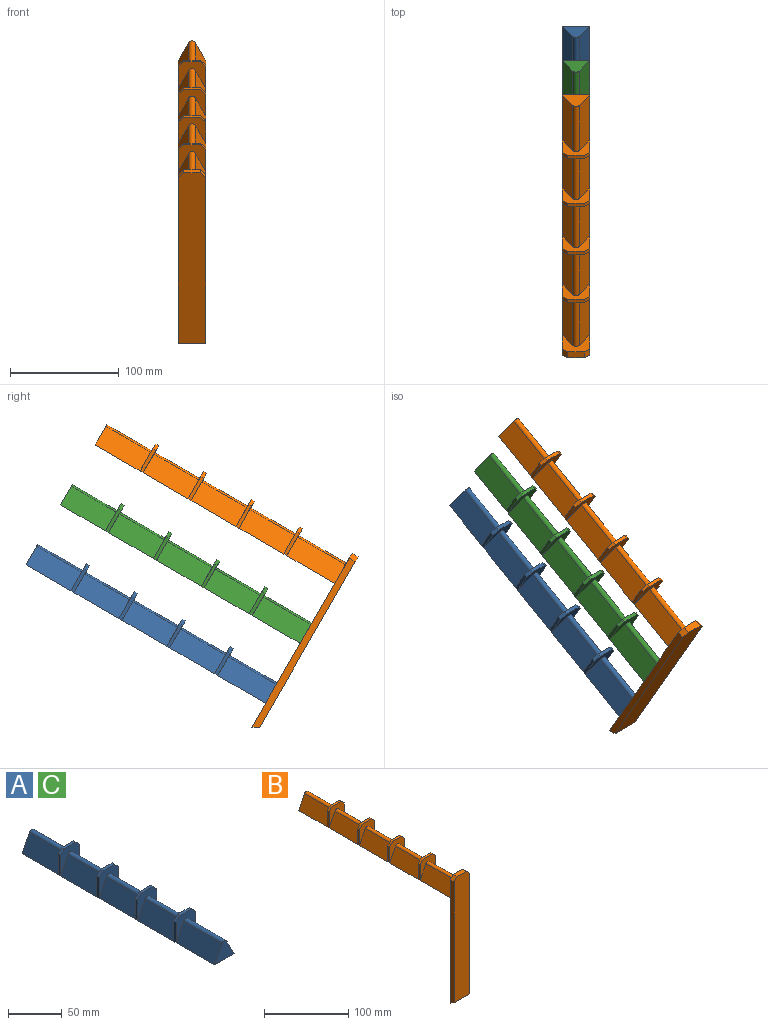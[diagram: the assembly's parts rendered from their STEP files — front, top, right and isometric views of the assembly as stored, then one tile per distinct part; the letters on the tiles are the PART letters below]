
ASSEMBLY  parts=3 mates=2
PART A: 46 faces, bbox 25.4x254x28.6 mm
  f0: plane 47.63x19.72mm, normal (0.89,0,0.45), area 1050mm2, adj f10,f23,f29,f33
  f1: plane 47.63x19.72mm, normal (-0.89,0,0.45), area 1050mm2, adj f10,f23,f29,f33
  f2: plane 47.63x19.72mm, normal (0.89,0,0.45), area 1050mm2, adj f10,f13,f24,f34
  f3: plane 47.63x19.72mm, normal (-0.89,0,0.45), area 1050mm2, adj f10,f13,f24,f34
  f4: plane 47.63x19.72mm, normal (0.89,0,0.45), area 1050mm2, adj f10,f19,f28,f35
  f5: plane 47.63x19.72mm, normal (-0.89,0,0.45), area 1050mm2, adj f10,f19,f28,f35
  f6: plane 50.8x19.72mm, normal (0.89,0,0.45), area 1120mm2, adj f8,f10,f14,f36
  f7: plane 50.8x19.72mm, normal (-0.89,0,0.45), area 1120mm2, adj f8,f10,f14,f36
  f8: plane 25.4x21.48mm, normal (0,-1,0), area 313.6mm2, adj f6,f7,f10,f36
  f9: plane 25.4x21.48mm, normal (0,1,0), area 313.6mm2, adj f10,f11,f12,f37
  f10: plane 254x25.4mm, normal (0,0,-1), area 6451.6mm2, adj f0,f1,f2,f3,f4,f5,f6,f7
  f11: plane 47.63x19.72mm, normal (0.89,0,0.45), area 1050mm2, adj f9,f10,f18,f37
  f12: plane 47.63x19.72mm, normal (-0.89,0,0.45), area 1050mm2, adj f9,f10,f18,f37
  f13: plane 28.58x25.4mm, normal (0,1,0), area 386.4mm2, adj f2,f3,f15,f16,f17,f34,f44,f45
  f14: plane 28.58x25.4mm, normal (0,-1,0), area 386.4mm2, adj f6,f7,f15,f16,f17,f36,f44,f45
  f15: plane 23.5x3.18mm, normal (-1,0,0), area 74.6mm2, adj f10,f13,f14,f45
  f16: plane 23.5x3.18mm, normal (1,0,0), area 74.6mm2, adj f10,f13,f14,f44
  f17: plane 15.24x3.18mm, normal (0,0,1), area 48.4mm2, adj f13,f14,f44,f45
  f18: plane 28.58x25.4mm, normal (0,1,0), area 386.4mm2, adj f11,f12,f20,f21,f22,f37,f40,f41
  f19: plane 28.58x25.4mm, normal (0,-1,0), area 386.4mm2, adj f4,f5,f20,f21,f22,f35,f40,f41
  f20: plane 23.5x3.18mm, normal (-1,0,0), area 74.6mm2, adj f10,f18,f19,f41
  f21: plane 23.5x3.18mm, normal (1,0,0), area 74.6mm2, adj f10,f18,f19,f40
  f22: plane 15.24x3.18mm, normal (0,0,1), area 48.4mm2, adj f18,f19,f40,f41
  f23: plane 28.58x25.4mm, normal (0,1,0), area 386.4mm2, adj f0,f1,f25,f26,f27,f33,f42,f43
  f24: plane 28.58x25.4mm, normal (0,-1,0), area 386.4mm2, adj f2,f3,f25,f26,f27,f34,f42,f43
  f25: plane 23.5x3.18mm, normal (-1,0,0), area 74.6mm2, adj f10,f23,f24,f43
  f26: plane 23.5x3.18mm, normal (1,0,0), area 74.6mm2, adj f10,f23,f24,f42
  f27: plane 15.24x3.18mm, normal (0,0,1), area 48.4mm2, adj f23,f24,f42,f43
  f28: plane 28.58x25.4mm, normal (0,1,0), area 386.4mm2, adj f4,f5,f30,f31,f32,f35,f38,f39
  f29: plane 28.58x25.4mm, normal (0,-1,0), area 386.4mm2, adj f0,f1,f30,f31,f32,f33,f38,f39
  f30: plane 23.5x3.18mm, normal (-1,0,0), area 74.6mm2, adj f10,f28,f29,f39
  f31: plane 23.5x3.18mm, normal (1,0,0), area 74.6mm2, adj f10,f28,f29,f38
  f32: plane 15.24x3.18mm, normal (0,0,1), area 48.4mm2, adj f28,f29,f38,f39
  f33: cylinder r=3.17mm len=47.63mm, axis (0,-1,0), area 334.8mm2, adj f0,f1,f23,f29
  f34: cylinder r=3.17mm len=47.63mm, axis (0,-1,0), area 334.8mm2, adj f2,f3,f13,f24
  f35: cylinder r=3.17mm len=47.63mm, axis (0,-1,0), area 334.8mm2, adj f4,f5,f19,f28
  f36: cylinder r=3.17mm len=50.8mm, axis (0,-1,0), area 357.1mm2, adj f6,f7,f8,f14
  f37: cylinder r=3.17mm len=47.63mm, axis (0,-1,0), area 334.8mm2, adj f9,f11,f12,f18
  f38: plane 5.08x5.08mm, normal (0.71,0,0.71), area 22.8mm2, adj f28,f29,f31,f32
  f39: plane 5.08x5.08mm, normal (-0.71,0,0.71), area 22.8mm2, adj f28,f29,f30,f32
  f40: plane 5.08x5.08mm, normal (0.71,0,0.71), area 22.8mm2, adj f18,f19,f21,f22
  f41: plane 5.08x5.08mm, normal (-0.71,0,0.71), area 22.8mm2, adj f18,f19,f20,f22
  f42: plane 5.08x5.08mm, normal (0.71,0,0.71), area 22.8mm2, adj f23,f24,f26,f27
  f43: plane 5.08x5.08mm, normal (-0.71,0,0.71), area 22.8mm2, adj f23,f24,f25,f27
  f44: plane 5.08x5.08mm, normal (0.71,0,0.71), area 22.8mm2, adj f13,f14,f16,f17
  f45: plane 5.08x5.08mm, normal (-0.71,0,0.71), area 22.8mm2, adj f13,f14,f15,f17
PART B: 54 faces, bbox 25.4x260.4x184.2 mm
  f0: plane 179.07x6.35mm, normal (1,0,0), area 1125.5mm2, adj f39,f40,f50,f52,f53
  f1: plane 254x25.4mm, normal (0,0,-1), area 6451.6mm2, adj f2,f3,f4,f5,f6,f7,f8,f9
  f2: plane 47.63x19.72mm, normal (0.89,0,0.45), area 1050mm2, adj f1,f23,f29,f33
  f3: plane 47.63x19.72mm, normal (-0.89,0,0.45), area 1050mm2, adj f1,f23,f29,f33
  f4: plane 47.63x19.72mm, normal (0.89,0,0.45), area 1050mm2, adj f1,f13,f24,f34
  f5: plane 47.63x19.72mm, normal (-0.89,0,0.45), area 1050mm2, adj f1,f13,f24,f34
  f6: plane 47.63x19.72mm, normal (0.89,0,0.45), area 1050mm2, adj f1,f19,f28,f35
  f7: plane 47.63x19.72mm, normal (-0.89,0,0.45), area 1050mm2, adj f1,f19,f28,f35
  f8: plane 50.8x19.72mm, normal (0.89,0,0.45), area 1120mm2, adj f1,f14,f36,f40
  f9: plane 50.8x19.72mm, normal (-0.89,0,0.45), area 1120mm2, adj f1,f14,f36,f40
  f10: plane 25.4x21.48mm, normal (0,1,0), area 313.6mm2, adj f1,f11,f12,f37
  f11: plane 47.63x19.72mm, normal (0.89,0,0.45), area 1050mm2, adj f1,f10,f18,f37
  f12: plane 47.63x19.72mm, normal (-0.89,0,0.45), area 1050mm2, adj f1,f10,f18,f37
  f13: plane 28.58x25.4mm, normal (0,1,0), area 386.4mm2, adj f4,f5,f15,f16,f17,f34,f48,f49
  f14: plane 28.58x25.4mm, normal (0,-1,0), area 386.4mm2, adj f8,f9,f15,f16,f17,f36,f48,f49
  f15: plane 23.5x3.18mm, normal (-1,0,0), area 74.6mm2, adj f1,f13,f14,f49
  f16: plane 23.5x3.18mm, normal (1,0,0), area 74.6mm2, adj f1,f13,f14,f48
  f17: plane 15.24x3.18mm, normal (0,0,1), area 48.4mm2, adj f13,f14,f48,f49
  f18: plane 28.58x25.4mm, normal (0,1,0), area 386.4mm2, adj f11,f12,f20,f21,f22,f37,f44,f45
  f19: plane 28.58x25.4mm, normal (0,-1,0), area 386.4mm2, adj f6,f7,f20,f21,f22,f35,f44,f45
  f20: plane 23.5x3.18mm, normal (-1,0,0), area 74.6mm2, adj f1,f18,f19,f45
  f21: plane 23.5x3.18mm, normal (1,0,0), area 74.6mm2, adj f1,f18,f19,f44
  f22: plane 15.24x3.18mm, normal (0,0,1), area 48.4mm2, adj f18,f19,f44,f45
  f23: plane 28.58x25.4mm, normal (0,1,0), area 386.4mm2, adj f2,f3,f25,f26,f27,f33,f46,f47
  f24: plane 28.58x25.4mm, normal (0,-1,0), area 386.4mm2, adj f4,f5,f25,f26,f27,f34,f46,f47
  f25: plane 23.5x3.18mm, normal (-1,0,0), area 74.6mm2, adj f1,f23,f24,f47
  f26: plane 23.5x3.18mm, normal (1,0,0), area 74.6mm2, adj f1,f23,f24,f46
  f27: plane 15.24x3.18mm, normal (0,0,1), area 48.4mm2, adj f23,f24,f46,f47
  f28: plane 28.58x25.4mm, normal (0,1,0), area 386.4mm2, adj f6,f7,f30,f31,f32,f35,f42,f43
  f29: plane 28.58x25.4mm, normal (0,-1,0), area 386.4mm2, adj f2,f3,f30,f31,f32,f33,f42,f43
  f30: plane 23.5x3.18mm, normal (-1,0,0), area 74.6mm2, adj f1,f28,f29,f43
  f31: plane 23.5x3.18mm, normal (1,0,0), area 74.6mm2, adj f1,f28,f29,f42
  f32: plane 15.24x3.18mm, normal (0,0,1), area 48.4mm2, adj f28,f29,f42,f43
  f33: cylinder r=3.17mm len=47.63mm, axis (0,-1,0), area 334.8mm2, adj f2,f3,f23,f29
  f34: cylinder r=3.17mm len=47.63mm, axis (0,-1,0), area 334.8mm2, adj f4,f5,f13,f24
  f35: cylinder r=3.17mm len=47.63mm, axis (0,-1,0), area 334.8mm2, adj f6,f7,f19,f28
  f36: cylinder r=3.17mm len=50.8mm, axis (0,-1,0), area 357.1mm2, adj f8,f9,f14,f40
  f37: cylinder r=3.17mm len=47.63mm, axis (0,-1,0), area 334.8mm2, adj f10,f11,f12,f18
  f38: plane 179.07x6.35mm, normal (-1,0,0), area 1125.5mm2, adj f39,f40,f51,f52,f53
  f39: plane 180.48x25.4mm, normal (0,-1,0), area 4558.5mm2, adj f0,f38,f41,f50,f51,f53
  f40: plane 31.75x25.4mm, normal (0,1,0), area 467.1mm2, adj f0,f8,f9,f36,f38,f41,f50,f51
  f41: plane 15.24x6.35mm, normal (0,0,1), area 96.8mm2, adj f39,f40,f50,f51
  f42: plane 5.08x5.08mm, normal (0.71,0,0.71), area 22.8mm2, adj f28,f29,f31,f32
  f43: plane 5.08x5.08mm, normal (-0.71,0,0.71), area 22.8mm2, adj f28,f29,f30,f32
  f44: plane 5.08x5.08mm, normal (0.71,0,0.71), area 22.8mm2, adj f18,f19,f21,f22
  f45: plane 5.08x5.08mm, normal (-0.71,0,0.71), area 22.8mm2, adj f18,f19,f20,f22
  f46: plane 5.08x5.08mm, normal (0.71,0,0.71), area 22.8mm2, adj f23,f24,f26,f27
  f47: plane 5.08x5.08mm, normal (-0.71,0,0.71), area 22.8mm2, adj f23,f24,f25,f27
  f48: plane 5.08x5.08mm, normal (0.71,0,0.71), area 22.8mm2, adj f13,f14,f16,f17
  f49: plane 5.08x5.08mm, normal (-0.71,0,0.71), area 22.8mm2, adj f13,f14,f15,f17
  f50: plane 6.35x5.08mm, normal (0.71,0,0.71), area 45.6mm2, adj f0,f39,f40,f41
  f51: plane 6.35x5.08mm, normal (-0.71,0,0.71), area 45.6mm2, adj f38,f39,f40,f41
  f52: plane 152.4x25.4mm, normal (0,1,0), area 3871mm2, adj f0,f1,f38,f53
  f53: plane 25.4x6.35mm, normal (0,-0.5,-0.87), area 186.2mm2, adj f0,f38,f39,f52
PART C: same geometry as A
PLACE A rot(axis=(1,0,0),30deg) t=(-94.42,126.31,103.51)mm
PLACE B rot(axis=(1,0,0),30deg) t=(-94.42,62.81,213.49)mm
PLACE C rot(axis=(1,0,0),30deg) t=(-94.42,94.56,158.5)mm
MATE fastened C.f8 <-> B.f52  axis (0,-0.87,-0.5) through (-156.35,-41.58,79.9)mm
MATE fastened A.f8 <-> B.f52  axis (0,-0.87,-0.5) through (-156.35,-9.83,24.91)mm
